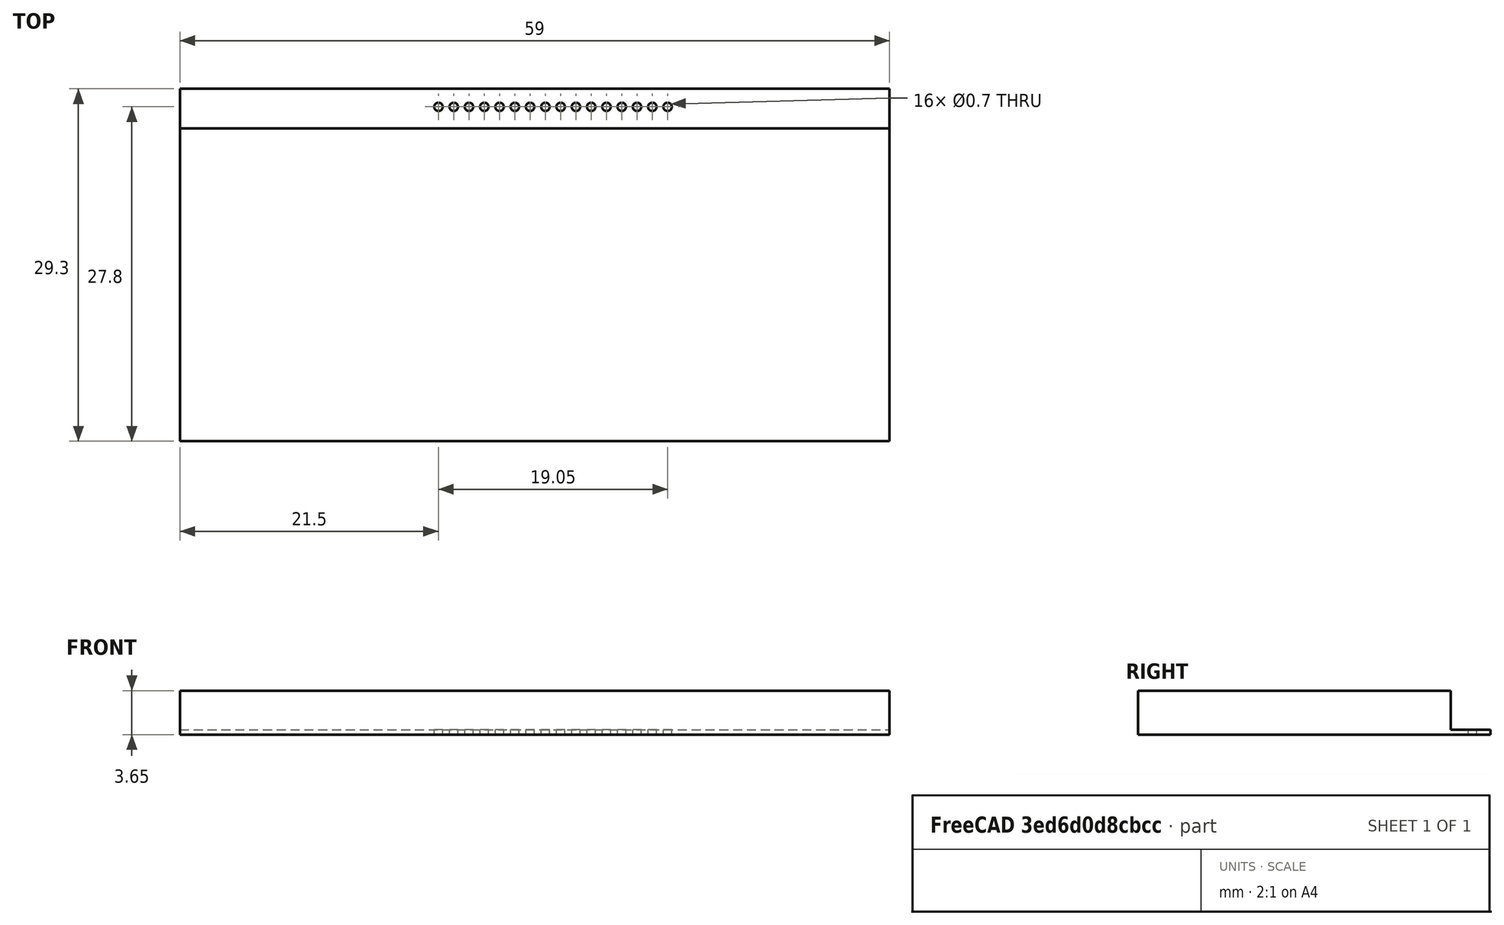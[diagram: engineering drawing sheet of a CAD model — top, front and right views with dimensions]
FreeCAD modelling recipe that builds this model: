
FCSTD DOCUMENT  (FreeCAD 0.16R)
Label: wh1602s
License: All rights reserved
LicenseURL: http://en.wikipedia.org/wiki/All_rights_reserved
objects: Part::Box×6, Part::Cut×3, Part::Cylinder×1, Part::FeaturePython×1, Part::MultiFuse×1
note: 12 computed .brp shape members not serialized (recipe doc carries the construction recipe); baked Part::Feature solids carry a one-line shape summary decoded from their .brp

FEATURE [Part::Box] Box  label="Куб"
  Height = 0.4
  Length = 59
  Width = 29.3
FEATURE [Part::Box] Box001  label="Куб001"
  Height = 3.25
  Length = 59
  Placement = pos=(0,0,0.4) rot=(0,0,1;0rad)
  Width = 26
FEATURE [Part::Box] Box002  label="Куб002"
  Height = 3.25
  Length = 56.3
  Placement = pos=(1.35,4.1,0.4) rot=(0,0,1;0rad)
  Width = 19.4
FEATURE [Part::Cut] Cut
  Base = -> Box001
  Tool = -> Box002
FEATURE [Part::Box] Box003  label="Куб003"
  Height = 3.25
  Length = 56.3
  Placement = pos=(1.35,4.1,0.4) rot=(0,0,1;0rad)
  Width = 19.4
FEATURE [Part::Cylinder] Cylinder  label="Цилиндр"
  Angle = 360
  Height = 0.4
  Placement = pos=(21.5,27.8,0) rot=(0,0,1;0rad)
  Radius = 0.35
FEATURE [Part::Box] Box004  label="Куб004"
  Height = 3.25
  Length = 52
  Placement = pos=(3.5,6.3,0.4) rot=(0,0,1;0rad)
  Width = 15
FEATURE [Part::Cut] Cut001
  Base = -> Box003
  Tool = -> Box004
FEATURE [Part::Box] Box005  label="box005"
  Height = 3.25
  Length = 52
  Placement = pos=(3.5,6.3,0.4) rot=(0,0,1;0rad)
  Width = 15
FEATURE [Part::FeaturePython] Array  # Draft array (typed FeaturePython)
  Angle = 360
  ArrayType = 0
  Axis = (0,0,1)
  Base = -> Cylinder
  Center = (0,0,0)
  Fuse = false
  IntervalAxis = (0,0,0)
  IntervalX = (1.27,0,0)
  IntervalY = (0,1,0)
  IntervalZ = (0,0,0)
  NumberPolar = 1
  NumberX = 16
  NumberY = 1
  NumberZ = 1
FEATURE [Part::Cut] Cut002
  Base = -> Box
  Tool = -> Array
FEATURE [Part::MultiFuse] Fusion
  Shapes = -> [Cut,Cut001,Box005,Cut002]
